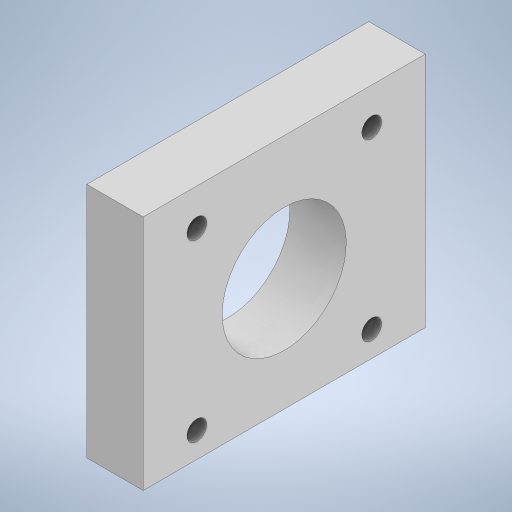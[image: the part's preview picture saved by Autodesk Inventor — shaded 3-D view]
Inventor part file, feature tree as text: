
AUTODESK INVENTOR PART (.ipt)
format: ipt  version: 2024 (Build 280153000, 153)  size: 241,152 bytes
history: native  units: mm
features: extrude x1, sketch x1
ambient origin geometry x8: Origin, YZ Plane, XZ Plane, XY Plane, X Axis, Y Axis, Z Axis, Center Point
bodies: Solido1 (feature_tree)
feature tree (2):
  extrude  "Estrusione1"  Depth=25.0mm
  sketch  "Schizzo1"
